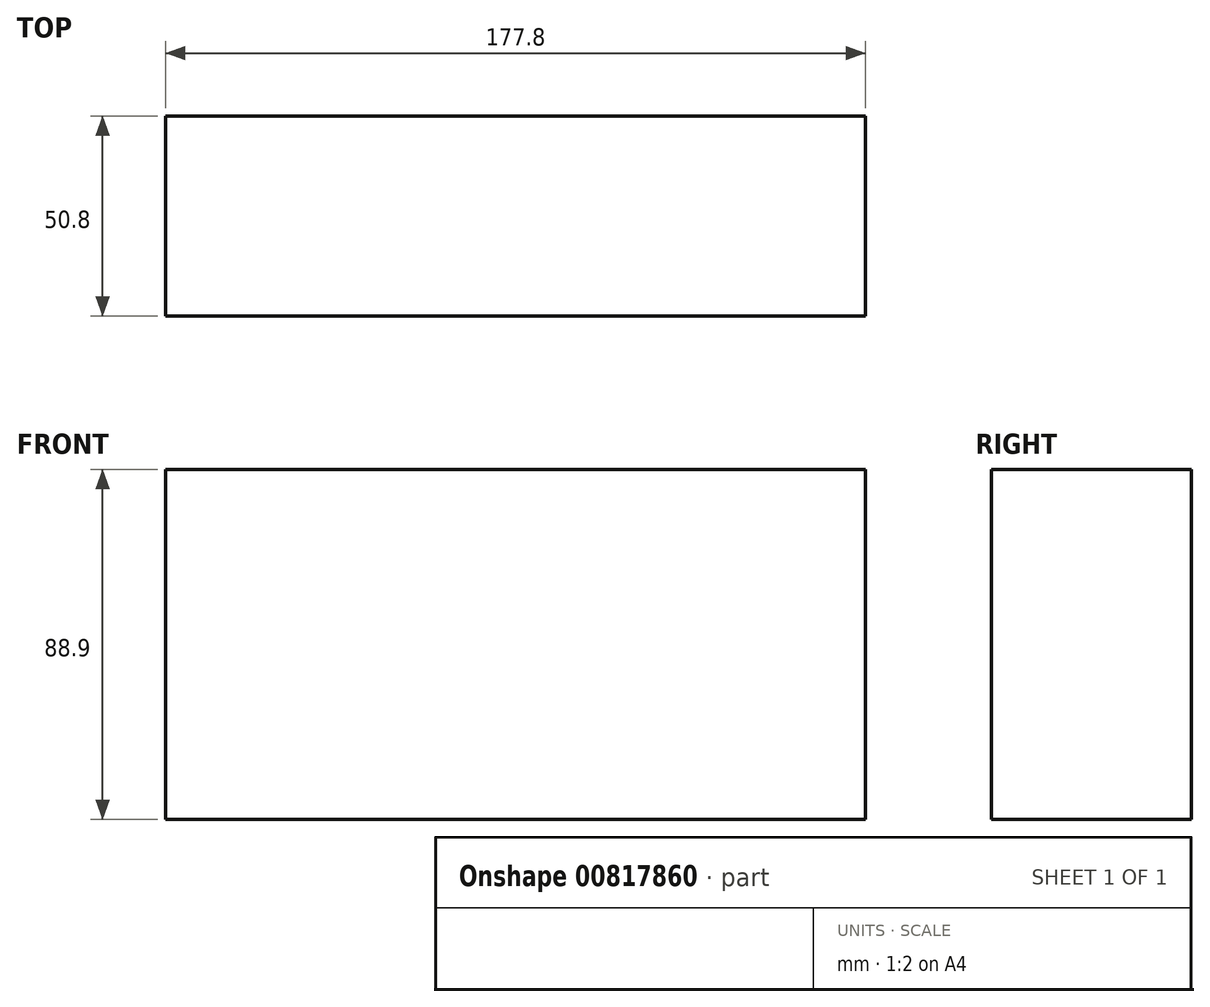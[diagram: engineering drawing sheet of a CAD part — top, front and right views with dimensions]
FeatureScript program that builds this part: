
annotation { "Feature Type Name" : "Feature", "Feature Type Description" : "" }
export const myFeature = defineFeature(function(context is Context, id is Id, definition is map)
    precondition{}
    {
        {
            var Q0;
            Q0=qCreatedBy(makeId("Front.planeOp"),FACE);
            var sketch = newSketch(context, id + "F0", { "sketchPlane" : qUnion([Q0])});
            skLineSegment(sketch, "E0.bottom", {"start": v(0, 0) * mm, "end": v(1219.2, 0) * mm});
            skLineSegment(sketch, "E0.top", {"start": v(0, -1524) * mm, "end": v(1219.2, -1524) * mm});
            skLineSegment(sketch, "E0.left", {"start": v(0, 0) * mm, "end": v(0, -1524) * mm});
            skLineSegment(sketch, "E0.right", {"start": v(1219.2, 0) * mm, "end": v(1219.2, -1524) * mm});
            skSolve(sketch);
        }
        {
            var Q0;
            Q0=makeQuery(id+"F0.imprint","IMPRINT",FACE,{"disambiguationData":[TD([[makeQuery(id+"F0.imprint","IMPRINT",EDGE,{"derivedFrom":sQuery(id+"F0.wireOp",EDGE,"E0.bottom")}),-1.0]])]});
            var sketch = newSketch(context, id + "F1", { "sketchPlane" : qUnion([Q0])});
            skLineSegment(sketch, "E1.bottom", {"start": v(116.04, -271.51) * mm, "end": v(293.84, -271.51) * mm});
            skLineSegment(sketch, "E1.top", {"start": v(116.04, -360.41) * mm, "end": v(293.84, -360.41) * mm});
            skLineSegment(sketch, "E1.left", {"start": v(116.04, -271.51) * mm, "end": v(116.04, -360.41) * mm});
            skLineSegment(sketch, "E1.right", {"start": v(293.84, -271.51) * mm, "end": v(293.84, -360.41) * mm});
            skSolve(sketch);
        }
        {
            var Q0;
            Q0 = qSketchRegion(id + "F1", true);
            extrude(context, id + "F2", {"entities" : qUnion([Q0]), "depth" : 50.8 * mm, "offsetDistance" : 25.4 * mm});
        }
    });
